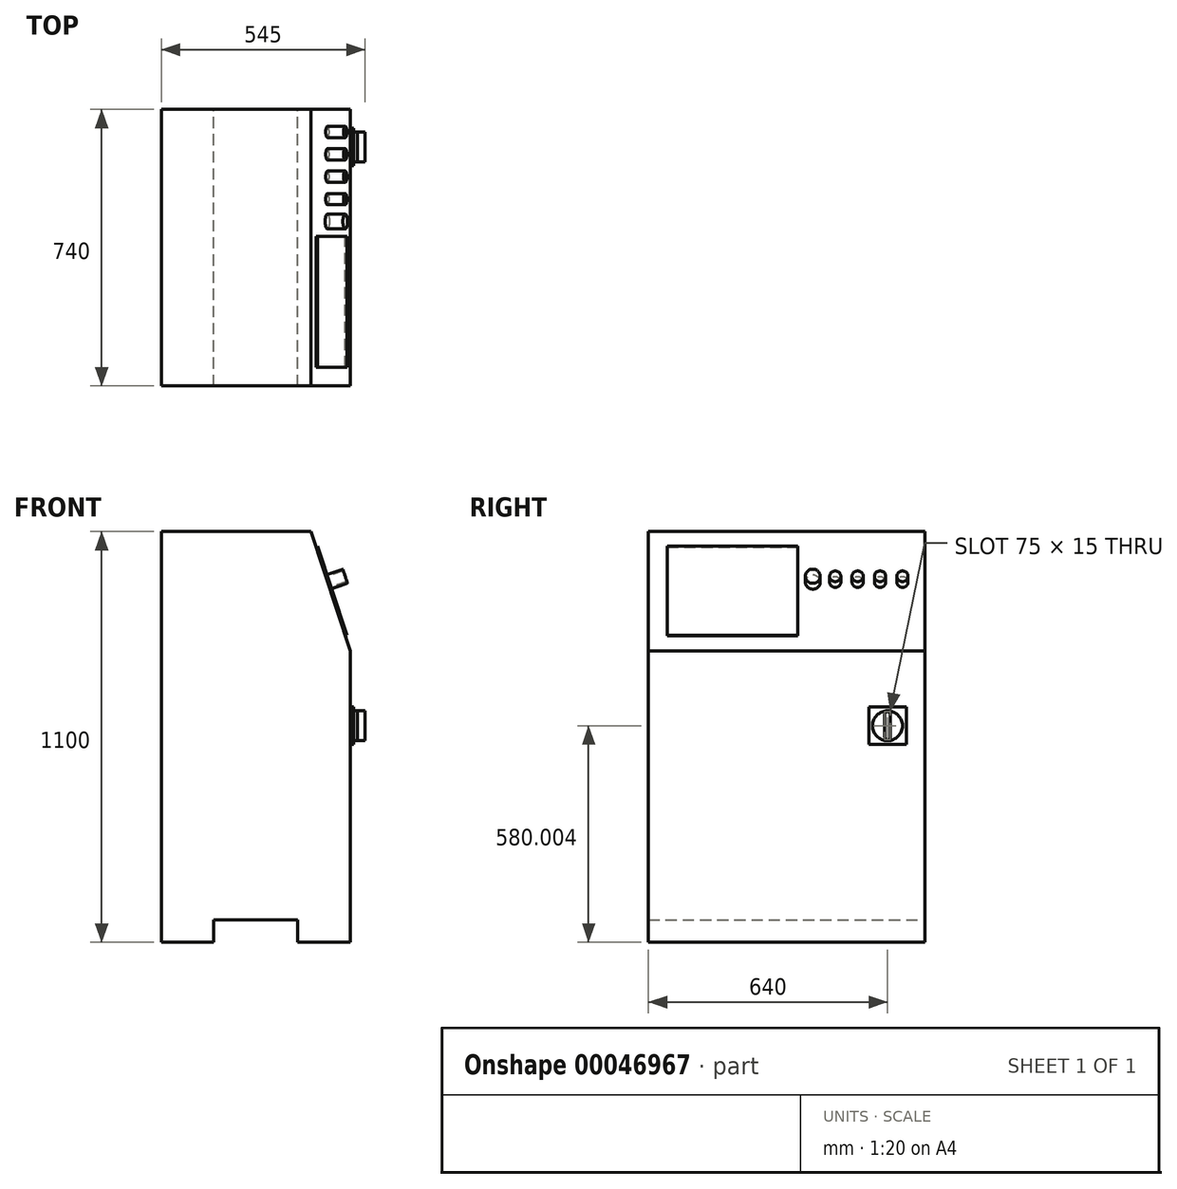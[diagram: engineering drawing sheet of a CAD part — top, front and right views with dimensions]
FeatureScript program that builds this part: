
annotation { "Feature Type Name" : "Feature", "Feature Type Description" : "" }
export const myFeature = defineFeature(function(context is Context, id is Id, definition is map)
    precondition{}
    {
        {
            var Q0;
            Q0=qCreatedBy(makeId("Front.planeOp"),FACE);
            var sketch = newSketch(context, id + "F0", { "sketchPlane" : qUnion([Q0])});
            skLineSegment(sketch, "E0", {"start": v(617.14, 766.1) * mm, "end": v(617.14, -333.9) * mm});
            skLineSegment(sketch, "E1", {"start": v(617.14, -333.9) * mm, "end": v(757.14, -333.9) * mm});
            skLineSegment(sketch, "E2", {"start": v(757.14, -333.9) * mm, "end": v(757.14, -273.9) * mm});
            skLineSegment(sketch, "E3", {"start": v(757.14, -273.9) * mm, "end": v(982.14, -273.9) * mm});
            skLineSegment(sketch, "E4", {"start": v(982.14, -273.9) * mm, "end": v(982.14, -333.9) * mm});
            skLineSegment(sketch, "E5", {"start": v(982.14, -333.9) * mm, "end": v(1122.14, -333.9) * mm});
            skLineSegment(sketch, "E6", {"start": v(1122.14, -333.9) * mm, "end": v(1122.14, 446.1) * mm});
            skLineSegment(sketch, "E7", {"start": v(1122.14, 446.1) * mm, "end": v(1017.14, 766.1) * mm});
            skLineSegment(sketch, "E8", {"start": v(1017.14, 766.1) * mm, "end": v(617.14, 766.1) * mm});
            skSolve(sketch);
        }
        {
            var Q0;
            Q0=makeQuery(id+"F0.imprint","IMPRINT",FACE,{"disambiguationData":[TD([[makeQuery(id+"F0.imprint","IMPRINT",EDGE,{"derivedFrom":sQuery(id+"F0.wireOp",EDGE,"E0")}),1.0]])]});
            extrude(context, id + "F1", {"entities" : qUnion([Q0]), "depth" : 740 * mm});
        }
        {
            var Q0;
            Q0=makeQuery(id+"F1.opExtrude","SWEPT_FACE",FACE,{"disambiguationData":[OSD([sQuery(id+"F0.wireOp",EDGE,"E6")])]});
            var sketch = newSketch(context, id + "F2", { "sketchPlane" : qUnion([Q0])});
            skLineSegment(sketch, "E9.bottom", {"start": v(-150, 296.1) * mm, "end": v(-50, 296.1) * mm});
            skLineSegment(sketch, "E9.top", {"start": v(-150, 196.1) * mm, "end": v(-50, 196.1) * mm});
            skLineSegment(sketch, "E9.left", {"start": v(-150, 296.1) * mm, "end": v(-150, 196.1) * mm});
            skLineSegment(sketch, "E9.right", {"start": v(-50, 296.1) * mm, "end": v(-50, 196.1) * mm});
            skLineSegment(sketch, "E10", {"start": v(-50, 296.1) * mm, "end": v(-150, 196.1) * mm, "construction": true});
            skLineSegment(sketch, "E11", {"start": v(-150, 296.1) * mm, "end": v(-50, 196.1) * mm, "construction": true});
            skCircle(sketch, "E12", {"center": v(-100, 246.1) * mm, "radius": 40 * mm});
            skLineSegment(sketch, "E13", {"start": v(-100, 276.1) * mm, "end": v(-100, 216.1) * mm, "construction": true});
            skArc(sketch, "E14.0.startCap", {"start": v(-107.5, 276.1) * mm, "mid": v(-100, 283.6) * mm, "end": v(-92.5, 276.1) * mm});
            skArc(sketch, "E14.0.endCap", {"start": v(-92.5, 216.1) * mm, "mid": v(-100, 208.6) * mm, "end": v(-107.5, 216.1) * mm});
            skLineSegment(sketch, "E14.0.left", {"start": v(-92.5, 276.1) * mm, "end": v(-92.5, 216.1) * mm});
            skLineSegment(sketch, "E14.0.right", {"start": v(-107.5, 276.1) * mm, "end": v(-107.5, 216.1) * mm});
            skArc(sketch, "E15.0.startCap", {"start": v(-107.5, 276.1) * mm, "mid": v(-100, 283.6) * mm, "end": v(-92.5, 276.1) * mm, "construction": true});
            skArc(sketch, "E15.0.endCap", {"start": v(-92.5, 216.1) * mm, "mid": v(-100, 208.6) * mm, "end": v(-107.5, 216.1) * mm, "construction": true});
            skLineSegment(sketch, "E15.0.left", {"start": v(-92.5, 276.1) * mm, "end": v(-92.5, 216.1) * mm, "construction": true});
            skLineSegment(sketch, "E15.0.right", {"start": v(-107.5, 276.1) * mm, "end": v(-107.5, 216.1) * mm, "construction": true});
            skSolve(sketch);
        }
        {
            var Q0;
            Q0=qSketchRegion(id+"F2",true);
            extrude(context, id + "F3", {"entities" : qUnion([Q0]), "operationType" : NewBodyOperationType.ADD, "depth" : 10 * mm});
        }
        {
            var Q0;
            Q0=makeQuery(id+"F2.imprint","IMPRINT",FACE,{"disambiguationData":[TD([[makeQuery(id+"F2.imprint","IMPRINT",EDGE,{"derivedFrom":sQuery(id+"F2.wireOp",EDGE,"E12")}),1.0]])]});
            extrude(context, id + "F4", {"entities" : qUnion([Q0]), "operationType" : NewBodyOperationType.ADD, "depth" : 20 * mm});
        }
        {
            var Q0;
            Q0=makeQuery(id+"F2.imprint","IMPRINT",FACE,{"disambiguationData":[TD([[makeQuery(id+"F2.imprint","IMPRINT",EDGE,{"derivedFrom":sQuery(id+"F2.wireOp",EDGE,"E14.0.startCap")}),-1.0]])]});
            extrude(context, id + "F5", {"entities" : qUnion([Q0]), "depth" : 40 * mm});
        }
        {
            var Q0;
            Q0=makeQuery(id+"F1.opExtrude","SWEPT_FACE",FACE,{"disambiguationData":[OSD([sQuery(id+"F0.wireOp",EDGE,"E7")])]});
            var sketch = newSketch(context, id + "F6", { "sketchPlane" : qUnion([Q0])});
            skLineSegment(sketch, "E16.bottom", {"start": v(-690, 367.4) * mm, "end": v(-340, 367.4) * mm});
            skLineSegment(sketch, "E16.top", {"start": v(-690, 117.4) * mm, "end": v(-340, 117.4) * mm});
            skLineSegment(sketch, "E16.left", {"start": v(-690, 367.4) * mm, "end": v(-690, 117.4) * mm});
            skLineSegment(sketch, "E16.right", {"start": v(-340, 367.4) * mm, "end": v(-340, 117.4) * mm});
            skLineSegment(sketch, "E17", {"start": v(-690, 367.4) * mm, "end": v(-690, 410.8) * mm, "construction": true});
            skLineSegment(sketch, "E18", {"start": v(-690, 117.4) * mm, "end": v(-690, 74.01) * mm, "construction": true});
            skSolve(sketch);
        }
        {
            var Q0;
            Q0=qSketchRegion(id+"F6",true);
            extrude(context, id + "F7", {"entities" : qUnion([Q0]), "depth" : 5 * mm});
        }
        {
            var Q0;
            Q0=makeQuery(id+"F1.opExtrude","SWEPT_FACE",FACE,{"disambiguationData":[OSD([sQuery(id+"F0.wireOp",EDGE,"E7")])]});
            var sketch = newSketch(context, id + "F8", { "sketchPlane" : qUnion([Q0])});
            skLineSegment(sketch, "E19", {"start": v(-300, 268.35) * mm, "end": v(0, 268.35) * mm, "construction": true});
            skCircle(sketch, "E20", {"center": v(-300, 268.35) * mm, "radius": 20 * mm});
            skCircle(sketch, "E21", {"center": v(-240, 268.35) * mm, "radius": 15 * mm});
            skCircle(sketch, "E22", {"center": v(-180, 268.35) * mm, "radius": 15 * mm});
            skCircle(sketch, "E23", {"center": v(-120, 268.35) * mm, "radius": 15 * mm});
            skCircle(sketch, "E24", {"center": v(-60, 268.35) * mm, "radius": 15 * mm});
            skSolve(sketch);
        }
        {
            var Q0;
            Q0=qSketchRegion(id+"F8",true);
            extrude(context, id + "F9", {"entities" : qUnion([Q0]), "depth" : 50 * mm});
        }
    });
